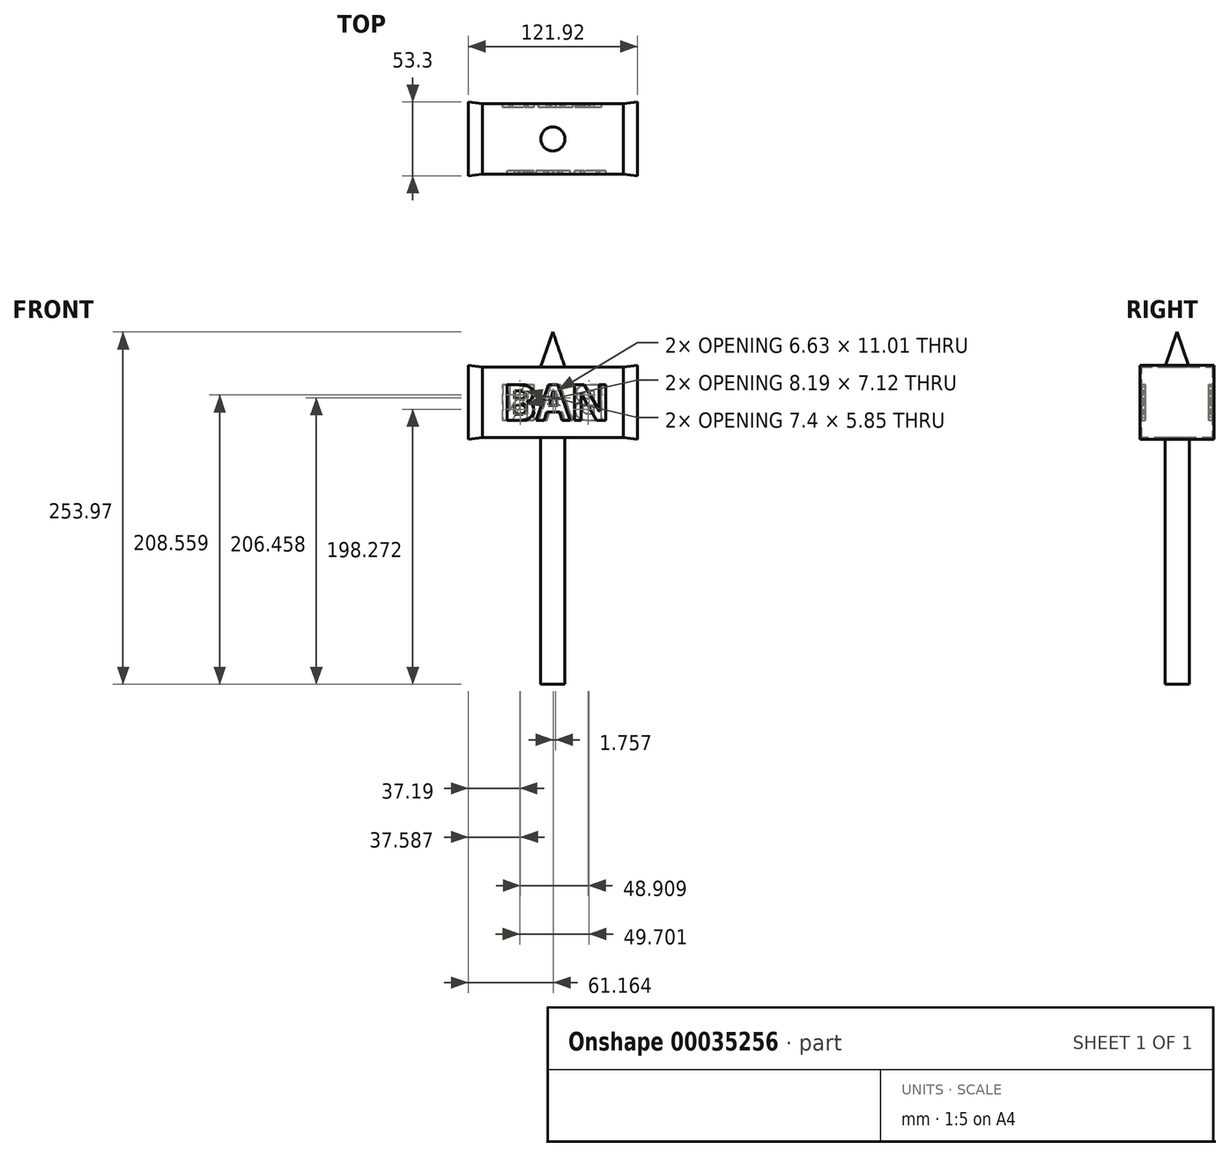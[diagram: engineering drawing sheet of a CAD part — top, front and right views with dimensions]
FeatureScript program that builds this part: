
annotation { "Feature Type Name" : "Feature", "Feature Type Description" : "" }
export const myFeature = defineFeature(function(context is Context, id is Id, definition is map)
    precondition{}
    {
        {
            var Q0;
            Q0=qCreatedBy(makeId("Right.planeOp"),FACE);
            var sketch = newSketch(context, id + "F0", { "sketchPlane" : qUnion([Q0])});
            skLineSegment(sketch, "E0.bottom", {"start": v(-25.4, 25.4) * mm, "end": v(25.4, 25.4) * mm});
            skLineSegment(sketch, "E0.top", {"start": v(-25.4, -25.4) * mm, "end": v(25.4, -25.4) * mm});
            skLineSegment(sketch, "E0.left", {"start": v(-25.4, 25.4) * mm, "end": v(-25.4, -25.4) * mm});
            skLineSegment(sketch, "E0.right", {"start": v(25.4, 25.4) * mm, "end": v(25.4, -25.4) * mm});
            skSolve(sketch);
        }
        {
            var Q0;
            Q0 = qSketchRegion(id + "F0", true);
            extrude(context, id + "F1", {"entities" : qUnion([Q0]), "endBound" : BoundingType.SYMMETRIC, "depth" : 101.6 * mm});
        }
        {
            var Q0;
            Q0=makeQuery(id+"F1.opExtrude","SWEPT_FACE",FACE,{"disambiguationData":[OSD([sQuery(id+"F0.wireOp",EDGE,"E0.right")])]});
            var sketch = newSketch(context, id + "F2", { "sketchPlane" : qUnion([Q0])});
            skLineSegment(sketch, "E1", {"start": v(-50.8, 25.4) * mm, "end": v(-38.23, 12.83) * mm});
            skLineSegment(sketch, "E2.MirrorCS", {"start": v(50.8, 25.4) * mm, "end": v(38.23, 12.83) * mm});
            skLineSegment(sketch, "E3.MirrorCS", {"start": v(-50.8, -25.4) * mm, "end": v(-38.23, -12.83) * mm});
            skLineSegment(sketch, "E4.MirrorCS", {"start": v(50.8, -25.4) * mm, "end": v(36.07, -12.83) * mm});
            skText(sketch, "E5", { "text": "BAN\n", "fontName": "OpenSans-Bold.ttf"});
            const initialGuessF2  = {"E5": [-0.03823, -0.01283, 1, 0, 0.02566]};
            skSetInitialGuess(sketch, initialGuessF2);
            skSolve(sketch);
        }
        {
            var Q0;
            Q0 = qSketchRegion(id + "F2", true);
            extrude(context, id + "F3", {"entities" : qUnion([Q0]), "operationType" : NewBodyOperationType.REMOVE, "oppositeDirection" : true, "depth" : 2.54 * mm});
        }
        {
            var Q0;
            Q0=makeQuery(id+"F1.opExtrude","SWEPT_FACE",FACE,{"disambiguationData":[OSD([sQuery(id+"F0.wireOp",EDGE,"E0.left")])]});
            var sketch = newSketch(context, id + "F4", { "sketchPlane" : qUnion([Q0])});
            skLineSegment(sketch, "E6.0", {"start": v(50.8, 25.4) * mm, "end": v(38.23, 12.83) * mm});
            skLineSegment(sketch, "E7.0.7", {"start": v(20.72, 0.5) * mm, "end": v(20.72, 0.67) * mm});
            skLineSegment(sketch, "E8.0.5", {"start": v(-31.47, -6.44) * mm, "end": v(-31.35, -6.44) * mm});
            skLineSegment(sketch, "E8.0.12", {"start": v(-17.99, 6.41) * mm, "end": v(-18.14, 6.41) * mm});
            skPoint(sketch, "E9", {"position": v(-36.07, -12.83) * mm});
            skPoint(sketch, "E8.0.0.start.orphan", {"position": v(-29.21, -12.83) * mm});
            skPoint(sketch, "E8.0.9.end.orphan", {"position": v(-18.32, -12.83) * mm});
            skPoint(sketch, "E8.0.9.start.orphan", {"position": v(-13.5, -12.83) * mm});
            skPoint(sketch, "E10.0.1.end.orphan", {"position": v(-10.3, -12.83) * mm});
            skPoint(sketch, "E10.0.1.start.orphan", {"position": v(-4.49, -12.83) * mm});
            skPoint(sketch, "E7.0.3.end.orphan", {"position": v(18.68, -10.88) * mm});
            skPoint(sketch, "E7.0.2.end.orphan", {"position": v(25.51, -12.83) * mm});
            skPoint(sketch, "E7.0.2.start.orphan", {"position": v(35.03, -12.83) * mm});
            skPoint(sketch, "E10.0.5.end.orphan", {"position": v(8.47, -12.83) * mm});
            skPoint(sketch, "E10.0.5.start.orphan", {"position": v(14.29, -12.83) * mm});
            skText(sketch, "E11", { "text": "BAN", "fontName": "OpenSans-Bold.ttf"});
            const initialGuessF4  = {"E11": [-0.03607, -0.01283, 1, 0, 0.02566]};
            skSetInitialGuess(sketch, initialGuessF4);
            skSolve(sketch);
        }
        {
            var Q0;
            Q0 = qSketchRegion(id + "F4", true);
            extrude(context, id + "F5", {"entities" : qUnion([Q0]), "operationType" : NewBodyOperationType.REMOVE, "oppositeDirection" : true, "depth" : 2.54 * mm});
        }
        {
            var Q0;
            Q0=makeQuery(id+"F1.opExtrude","CAP_FACE",FACE,{"disambiguationData":[OSD([sQuery(id+"F0.wireOp",EDGE,"E0.bottom"),sQuery(id+"F0.wireOp",EDGE,"E0.top"),sQuery(id+"F0.wireOp",EDGE,"E0.left"),sQuery(id+"F0.wireOp",EDGE,"E0.right")])],"isStart":true});
            var sketch = newSketch(context, id + "F6", { "sketchPlane" : qUnion([Q0])});
            skLineSegment(sketch, "E12.0", {"start": v(25.4, 25.4) * mm, "end": v(-25.4, 25.4) * mm});
            skLineSegment(sketch, "E12.1", {"start": v(25.4, 25.4) * mm, "end": v(25.4, -25.4) * mm});
            skSolve(sketch);
        }
        {
            var Q0;
            Q0=makeQuery(id+"F6.imprint","IMPRINT",FACE,{"disambiguationData":[TD([[makeQuery(id+"F6.imprint","IMPRINT",EDGE,{"derivedFrom":sQuery(id+"F6.wireOp",EDGE,"E12.0")}),1.0]])]});
            extrude(context, id + "F7", {"entities" : qUnion([Q0]), "depth" : 10.16 * mm, "hasDraft" : true, "draftAngle" : 7 * degree});
        }
        {
            var Q0;
            Q0=makeQuery(id+"F1.opExtrude","CAP_FACE",FACE,{"disambiguationData":[OSD([sQuery(id+"F0.wireOp",EDGE,"E0.bottom"),sQuery(id+"F0.wireOp",EDGE,"E0.top"),sQuery(id+"F0.wireOp",EDGE,"E0.left"),sQuery(id+"F0.wireOp",EDGE,"E0.right")])],"isStart":false});
            extrude(context, id + "F8", {"entities" : qUnion([Q0]), "depth" : 10.16 * mm, "hasDraft" : true, "draftAngle" : 7 * degree});
        }
        {
            var Q0;
            Q0=makeQuery(id+"F1.opExtrude","SWEPT_FACE",FACE,{"disambiguationData":[OSD([sQuery(id+"F0.wireOp",EDGE,"E0.top")])]});
            var sketch = newSketch(context, id + "F9", { "sketchPlane" : qUnion([Q0])});
            skCircle(sketch, "E13", {"center": v(0, 0) * mm, "radius": 8.73 * mm});
            skSolve(sketch);
        }
        {
            var Q0;
            Q0 = qSketchRegion(id + "F9", true);
            extrude(context, id + "F10", {"entities" : qUnion([Q0]), "depth" : 177.8 * mm});
        }
        {
            var Q0;
            Q0=makeQuery(id+"F1.opExtrude","SWEPT_FACE",FACE,{"disambiguationData":[OSD([sQuery(id+"F0.wireOp",EDGE,"E0.bottom")])]});
            var sketch = newSketch(context, id + "F11", { "sketchPlane" : qUnion([Q0])});
            skCircle(sketch, "E14.0", {"center": v(0, 0) * mm, "radius": 8.73 * mm});
            skSolve(sketch);
        }
        {
            var Q0;
            Q0 = qSketchRegion(id + "F11", true);
            extrude(context, id + "F12", {"entities" : qUnion([Q0]), "depth" : 25.4 * mm, "hasDraft" : true, "draftAngle" : 19 * degree, "draftPullDirection" : true});
        }
        {
            var Q0;
            Q0=makeQuery(id+"F5.boolean.opBoolean","COPY",FACE,{"derivedFrom":makeQuery(id+"F5.opExtrude","CAP_FACE",FACE,{"disambiguationData":[OSD([sQuery(id+"F4.wireOp",EDGE,"E11.sketch_text.stroke-0"),sQuery(id+"F4.wireOp",EDGE,"E11.sketch_text.stroke-1"),sQuery(id+"F4.wireOp",EDGE,"E11.sketch_text.stroke-2"),sQuery(id+"F4.wireOp",EDGE,"E11.sketch_text.stroke-3"),sQuery(id+"F4.wireOp",EDGE,"E11.sketch_text.stroke-4"),sQuery(id+"F4.wireOp",EDGE,"E11.sketch_text.stroke-5"),sQuery(id+"F4.wireOp",EDGE,"E11.sketch_text.stroke-6"),sQuery(id+"F4.wireOp",EDGE,"E11.sketch_text.stroke-7"),sQuery(id+"F4.wireOp",EDGE,"E11.sketch_text.stroke-8"),sQuery(id+"F4.wireOp",EDGE,"E11.sketch_text.stroke-9"),sQuery(id+"F4.wireOp",EDGE,"E11.sketch_text.stroke-10"),sQuery(id+"F4.wireOp",EDGE,"E11.sketch_text.stroke-11"),sQuery(id+"F4.wireOp",EDGE,"E11.sketch_text.stroke-12"),sQuery(id+"F4.wireOp",EDGE,"E11.sketch_text.stroke-13"),sQuery(id+"F4.wireOp",EDGE,"E11.sketch_text.stroke-14"),sQuery(id+"F4.wireOp",EDGE,"E11.sketch_text.stroke-15"),sQuery(id+"F4.wireOp",EDGE,"E11.sketch_text.stroke-16"),sQuery(id+"F4.wireOp",EDGE,"E11.sketch_text.stroke-17"),sQuery(id+"F4.wireOp",EDGE,"E11.sketch_text.stroke-18"),sQuery(id+"F4.wireOp",EDGE,"E11.sketch_text.stroke-19"),sQuery(id+"F4.wireOp",EDGE,"E11.sketch_text.stroke-20"),sQuery(id+"F4.wireOp",EDGE,"E11.sketch_text.stroke-21"),sQuery(id+"F4.wireOp",EDGE,"E11.sketch_text.stroke-22"),sQuery(id+"F4.wireOp",EDGE,"E11.sketch_text.stroke-23"),sQuery(id+"F4.wireOp",EDGE,"E11.sketch_text.stroke-24")])],"isStart":false})});
            var sketch = newSketch(context, id + "F13", { "sketchPlane" : qUnion([Q0])});
            skLineSegment(sketch, "E15.0.0", {"start": v(-24.95, 12.61) * mm, "end": v(-32.86, 12.61) * mm});
            skLineSegment(sketch, "E15.0.1", {"start": v(-32.86, 12.61) * mm, "end": v(-32.86, -12.83) * mm});
            skLineSegment(sketch, "E15.0.2", {"start": v(-32.86, -12.83) * mm, "end": v(-23.35, -12.83) * mm});
            skFitSpline(sketch, "E15.0.3", {"points": [v(-23.35, -12.83) * mm, v(-19.03, -12.83) * mm, v(-16.52, -10.88) * mm]});
            skFitSpline(sketch, "E15.0.4", {"points": [v(-16.52, -10.88) * mm, v(-14, -8.93) * mm, v(-14, -5.45) * mm]});
            skFitSpline(sketch, "E15.0.5", {"points": [v(-14, -5.45) * mm, v(-14, -3) * mm, v(-15.07, -1.52) * mm]});
            skFitSpline(sketch, "E15.0.6", {"points": [v(-15.07, -1.52) * mm, v(-16.15, -0.04) * mm, v(-18.56, 0.5) * mm]});
            skLineSegment(sketch, "E15.0.7", {"start": v(-18.56, 0.5) * mm, "end": v(-18.56, 0.67) * mm});
            skFitSpline(sketch, "E15.0.8", {"points": [v(-18.56, 0.67) * mm, v(-16.79, 0.97) * mm, v(-15.72, 2.43) * mm]});
            skFitSpline(sketch, "E15.0.9", {"points": [v(-15.72, 2.43) * mm, v(-14.65, 3.9) * mm, v(-14.65, 6.17) * mm]});
            skFitSpline(sketch, "E15.0.10", {"points": [v(-14.65, 6.17) * mm, v(-14.65, 9.53) * mm, v(-17.1, 11.07) * mm]});
            skFitSpline(sketch, "E15.0.11", {"points": [v(-17.1, 11.07) * mm, v(-19.54, 12.61) * mm, v(-24.95, 12.61) * mm]});
            skLineSegment(sketch, "E16.0.0", {"start": v(4.8, -6.77) * mm, "end": v(6.65, -12.83) * mm});
            skLineSegment(sketch, "E16.0.1", {"start": v(6.65, -12.83) * mm, "end": v(12.46, -12.83) * mm});
            skLineSegment(sketch, "E16.0.2", {"start": v(12.46, -12.83) * mm, "end": v(3.45, 12.72) * mm});
            skLineSegment(sketch, "E16.0.3", {"start": v(3.45, 12.72) * mm, "end": v(-3.14, 12.72) * mm});
            skLineSegment(sketch, "E16.0.4", {"start": v(-3.14, 12.72) * mm, "end": v(-12.13, -12.83) * mm});
            skLineSegment(sketch, "E16.0.5", {"start": v(-12.13, -12.83) * mm, "end": v(-6.31, -12.83) * mm});
            skLineSegment(sketch, "E16.0.6", {"start": v(-6.31, -12.83) * mm, "end": v(-4.47, -6.77) * mm});
            skLineSegment(sketch, "E16.0.7", {"start": v(-4.47, -6.77) * mm, "end": v(4.8, -6.77) * mm});
            skLineSegment(sketch, "E17.0.0", {"start": v(31.37, -12.83) * mm, "end": v(38.23, -12.83) * mm});
            skLineSegment(sketch, "E17.0.1", {"start": v(38.23, -12.83) * mm, "end": v(38.23, 12.61) * mm});
            skLineSegment(sketch, "E17.0.2", {"start": v(38.23, 12.61) * mm, "end": v(33.37, 12.61) * mm});
            skLineSegment(sketch, "E17.0.3", {"start": v(33.37, 12.61) * mm, "end": v(33.37, 0.57) * mm});
            skFitSpline(sketch, "E17.0.4", {"points": [v(33.37, 0.57) * mm, v(33.37, -1.48) * mm, v(33.63, -6.44) * mm]});
            skLineSegment(sketch, "E17.0.5", {"start": v(33.63, -6.44) * mm, "end": v(33.51, -6.44) * mm});
            skLineSegment(sketch, "E17.0.6", {"start": v(33.51, -6.44) * mm, "end": v(22.47, 12.61) * mm});
            skLineSegment(sketch, "E17.0.7", {"start": v(22.47, 12.61) * mm, "end": v(15.66, 12.61) * mm});
            skLineSegment(sketch, "E17.0.8", {"start": v(15.66, 12.61) * mm, "end": v(15.66, -12.83) * mm});
            skLineSegment(sketch, "E17.0.9", {"start": v(15.66, -12.83) * mm, "end": v(20.48, -12.83) * mm});
            skLineSegment(sketch, "E17.0.10", {"start": v(20.48, -12.83) * mm, "end": v(20.48, -0.86) * mm});
            skFitSpline(sketch, "E17.0.11", {"points": [v(20.48, -0.86) * mm, v(20.48, 1.32) * mm, v(20.15, 6.41) * mm]});
            skLineSegment(sketch, "E17.0.12", {"start": v(20.15, 6.41) * mm, "end": v(20.3, 6.41) * mm});
            skLineSegment(sketch, "E17.0.13", {"start": v(20.3, 6.41) * mm, "end": v(31.37, -12.83) * mm});
            skLineSegment(sketch, "E18.0.0", {"start": v(-27.47, 2.53) * mm, "end": v(-24.34, 2.53) * mm});
            skFitSpline(sketch, "E18.0.1", {"points": [v(-24.34, 2.53) * mm, v(-22.15, 2.53) * mm, v(-21.16, 3.21) * mm]});
            skFitSpline(sketch, "E18.0.2", {"points": [v(-21.16, 3.21) * mm, v(-20.18, 3.9) * mm, v(-20.18, 5.46) * mm]});
            skFitSpline(sketch, "E18.0.3", {"points": [v(-20.18, 5.46) * mm, v(-20.18, 6.92) * mm, v(-21.25, 7.56) * mm]});
            skFitSpline(sketch, "E18.0.4", {"points": [v(-21.25, 7.56) * mm, v(-22.32, 8.19) * mm, v(-24.64, 8.19) * mm]});
            skLineSegment(sketch, "E18.0.5", {"start": v(-24.64, 8.19) * mm, "end": v(-27.47, 8.19) * mm});
            skLineSegment(sketch, "E18.0.6", {"start": v(-27.47, 8.19) * mm, "end": v(-27.47, 2.53) * mm});
            skLineSegment(sketch, "E19.0.0", {"start": v(-27.47, -1.74) * mm, "end": v(-27.47, -8.37) * mm});
            skLineSegment(sketch, "E19.0.1", {"start": v(-27.47, -8.37) * mm, "end": v(-23.96, -8.37) * mm});
            skFitSpline(sketch, "E19.0.2", {"points": [v(-23.96, -8.37) * mm, v(-21.73, -8.37) * mm, v(-20.67, -7.52) * mm]});
            skFitSpline(sketch, "E19.0.3", {"points": [v(-20.67, -7.52) * mm, v(-19.6, -6.67) * mm, v(-19.6, -4.91) * mm]});
            skFitSpline(sketch, "E19.0.4", {"points": [v(-19.6, -4.91) * mm, v(-19.6, -1.74) * mm, v(-24.13, -1.74) * mm]});
            skLineSegment(sketch, "E19.0.5", {"start": v(-24.13, -1.74) * mm, "end": v(-27.47, -1.74) * mm});
            skFitSpline(sketch, "E20.0.0", {"points": [v(3.51, -2.25) * mm, v(0.96, 5.98) * mm, v(0.64, 7.06) * mm]});
            skFitSpline(sketch, "E20.0.1", {"points": [v(0.64, 7.06) * mm, v(0.31, 8.14) * mm, v(0.17, 8.76) * mm]});
            skFitSpline(sketch, "E20.0.2", {"points": [v(0.17, 8.76) * mm, v(-0.4, 6.54) * mm, v(-3.11, -2.25) * mm]});
            skLineSegment(sketch, "E20.0.3", {"start": v(-3.11, -2.25) * mm, "end": v(3.51, -2.25) * mm});
            skSolve(sketch);
        }
        {
            var Q0;
            Q0 = qSketchRegion(id + "F13", true);
            extrude(context, id + "F14", {"entities" : qUnion([Q0]), "depth" : 2.54 * mm});
        }
        {
            var Q0;
            Q0=makeQuery(id+"F3.boolean.opBoolean","COPY",FACE,{"derivedFrom":makeQuery(id+"F3.opExtrude","CAP_FACE",FACE,{"disambiguationData":[OSD([sQuery(id+"F2.wireOp",EDGE,"E5.sketch_text.stroke-0"),sQuery(id+"F2.wireOp",EDGE,"E5.sketch_text.stroke-1"),sQuery(id+"F2.wireOp",EDGE,"E5.sketch_text.stroke-2"),sQuery(id+"F2.wireOp",EDGE,"E5.sketch_text.stroke-3"),sQuery(id+"F2.wireOp",EDGE,"E5.sketch_text.stroke-4"),sQuery(id+"F2.wireOp",EDGE,"E5.sketch_text.stroke-5"),sQuery(id+"F2.wireOp",EDGE,"E5.sketch_text.stroke-6"),sQuery(id+"F2.wireOp",EDGE,"E5.sketch_text.stroke-7"),sQuery(id+"F2.wireOp",EDGE,"E5.sketch_text.stroke-8"),sQuery(id+"F2.wireOp",EDGE,"E5.sketch_text.stroke-9"),sQuery(id+"F2.wireOp",EDGE,"E5.sketch_text.stroke-10"),sQuery(id+"F2.wireOp",EDGE,"E5.sketch_text.stroke-11"),sQuery(id+"F2.wireOp",EDGE,"E5.sketch_text.stroke-12"),sQuery(id+"F2.wireOp",EDGE,"E5.sketch_text.stroke-13"),sQuery(id+"F2.wireOp",EDGE,"E5.sketch_text.stroke-14"),sQuery(id+"F2.wireOp",EDGE,"E5.sketch_text.stroke-15"),sQuery(id+"F2.wireOp",EDGE,"E5.sketch_text.stroke-16"),sQuery(id+"F2.wireOp",EDGE,"E5.sketch_text.stroke-17"),sQuery(id+"F2.wireOp",EDGE,"E5.sketch_text.stroke-18"),sQuery(id+"F2.wireOp",EDGE,"E5.sketch_text.stroke-19"),sQuery(id+"F2.wireOp",EDGE,"E5.sketch_text.stroke-20"),sQuery(id+"F2.wireOp",EDGE,"E5.sketch_text.stroke-21"),sQuery(id+"F2.wireOp",EDGE,"E5.sketch_text.stroke-22"),sQuery(id+"F2.wireOp",EDGE,"E5.sketch_text.stroke-23"),sQuery(id+"F2.wireOp",EDGE,"E5.sketch_text.stroke-24")])],"isStart":false})});
            var sketch = newSketch(context, id + "F15", { "sketchPlane" : qUnion([Q0])});
            skLineSegment(sketch, "E21.0.0", {"start": v(-27.1, 12.61) * mm, "end": v(-35.03, 12.61) * mm});
            skLineSegment(sketch, "E21.0.1", {"start": v(-35.03, 12.61) * mm, "end": v(-35.03, -12.83) * mm});
            skLineSegment(sketch, "E21.0.2", {"start": v(-35.03, -12.83) * mm, "end": v(-25.51, -12.83) * mm});
            skFitSpline(sketch, "E21.0.3", {"points": [v(-25.51, -12.83) * mm, v(-21.2, -12.83) * mm, v(-18.68, -10.88) * mm]});
            skFitSpline(sketch, "E21.0.4", {"points": [v(-18.68, -10.88) * mm, v(-16.16, -8.93) * mm, v(-16.16, -5.45) * mm]});
            skFitSpline(sketch, "E21.0.5", {"points": [v(-16.16, -5.45) * mm, v(-16.16, -3) * mm, v(-17.24, -1.52) * mm]});
            skFitSpline(sketch, "E21.0.6", {"points": [v(-17.24, -1.52) * mm, v(-18.3, -0.04) * mm, v(-20.72, 0.5) * mm]});
            skLineSegment(sketch, "E21.0.7", {"start": v(-20.72, 0.5) * mm, "end": v(-20.72, 0.67) * mm});
            skFitSpline(sketch, "E21.0.8", {"points": [v(-20.72, 0.67) * mm, v(-18.95, 0.97) * mm, v(-17.88, 2.43) * mm]});
            skFitSpline(sketch, "E21.0.9", {"points": [v(-17.88, 2.43) * mm, v(-16.8, 3.9) * mm, v(-16.8, 6.17) * mm]});
            skFitSpline(sketch, "E21.0.10", {"points": [v(-16.8, 6.17) * mm, v(-16.8, 9.53) * mm, v(-19.25, 11.07) * mm]});
            skFitSpline(sketch, "E21.0.11", {"points": [v(-19.25, 11.07) * mm, v(-21.7, 12.61) * mm, v(-27.1, 12.61) * mm]});
            skLineSegment(sketch, "E22.0.0", {"start": v(-29.63, 8.19) * mm, "end": v(-29.63, 2.53) * mm});
            skLineSegment(sketch, "E22.0.1", {"start": v(-29.63, 2.53) * mm, "end": v(-26.5, 2.53) * mm});
            skFitSpline(sketch, "E22.0.2", {"points": [v(-26.5, 2.53) * mm, v(-24.3, 2.53) * mm, v(-23.33, 3.21) * mm]});
            skFitSpline(sketch, "E22.0.3", {"points": [v(-23.33, 3.21) * mm, v(-22.34, 3.9) * mm, v(-22.34, 5.46) * mm]});
            skFitSpline(sketch, "E22.0.4", {"points": [v(-22.34, 5.46) * mm, v(-22.34, 6.92) * mm, v(-23.41, 7.56) * mm]});
            skFitSpline(sketch, "E22.0.5", {"points": [v(-23.41, 7.56) * mm, v(-24.48, 8.19) * mm, v(-26.8, 8.19) * mm]});
            skLineSegment(sketch, "E22.0.6", {"start": v(-26.8, 8.19) * mm, "end": v(-29.63, 8.19) * mm});
            skLineSegment(sketch, "E23.0.0", {"start": v(-26.3, -1.74) * mm, "end": v(-29.63, -1.74) * mm});
            skLineSegment(sketch, "E23.0.1", {"start": v(-29.63, -1.74) * mm, "end": v(-29.63, -8.37) * mm});
            skLineSegment(sketch, "E23.0.2", {"start": v(-29.63, -8.37) * mm, "end": v(-26.12, -8.37) * mm});
            skFitSpline(sketch, "E23.0.3", {"points": [v(-26.12, -8.37) * mm, v(-23.9, -8.37) * mm, v(-22.83, -7.52) * mm]});
            skFitSpline(sketch, "E23.0.4", {"points": [v(-22.83, -7.52) * mm, v(-21.77, -6.67) * mm, v(-21.77, -4.91) * mm]});
            skFitSpline(sketch, "E23.0.5", {"points": [v(-21.77, -4.91) * mm, v(-21.77, -1.74) * mm, v(-26.3, -1.74) * mm]});
            skLineSegment(sketch, "E24.0.0", {"start": v(2.64, -6.77) * mm, "end": v(4.49, -12.83) * mm});
            skLineSegment(sketch, "E24.0.1", {"start": v(4.49, -12.83) * mm, "end": v(10.3, -12.83) * mm});
            skLineSegment(sketch, "E24.0.2", {"start": v(10.3, -12.83) * mm, "end": v(1.29, 12.72) * mm});
            skLineSegment(sketch, "E24.0.3", {"start": v(1.29, 12.72) * mm, "end": v(-5.3, 12.72) * mm});
            skLineSegment(sketch, "E24.0.4", {"start": v(-5.3, 12.72) * mm, "end": v(-14.29, -12.83) * mm});
            skLineSegment(sketch, "E24.0.5", {"start": v(-14.29, -12.83) * mm, "end": v(-8.47, -12.83) * mm});
            skLineSegment(sketch, "E24.0.6", {"start": v(-8.47, -12.83) * mm, "end": v(-6.63, -6.77) * mm});
            skLineSegment(sketch, "E24.0.7", {"start": v(-6.63, -6.77) * mm, "end": v(2.64, -6.77) * mm});
            skPoint(sketch, "E25.0", {"position": v(0, 0) * mm});
            skLineSegment(sketch, "E26.0.0", {"start": v(29.21, -12.83) * mm, "end": v(36.07, -12.83) * mm});
            skLineSegment(sketch, "E26.0.1", {"start": v(36.07, -12.83) * mm, "end": v(36.07, 12.61) * mm});
            skLineSegment(sketch, "E26.0.2", {"start": v(36.07, 12.61) * mm, "end": v(31.21, 12.61) * mm});
            skLineSegment(sketch, "E26.0.3", {"start": v(31.21, 12.61) * mm, "end": v(31.21, 0.57) * mm});
            skFitSpline(sketch, "E26.0.4", {"points": [v(31.21, 0.57) * mm, v(31.21, -1.48) * mm, v(31.47, -6.44) * mm]});
            skLineSegment(sketch, "E26.0.5", {"start": v(31.47, -6.44) * mm, "end": v(31.35, -6.44) * mm});
            skLineSegment(sketch, "E26.0.6", {"start": v(31.35, -6.44) * mm, "end": v(20.3, 12.61) * mm});
            skLineSegment(sketch, "E26.0.7", {"start": v(20.3, 12.61) * mm, "end": v(13.5, 12.61) * mm});
            skLineSegment(sketch, "E26.0.8", {"start": v(13.5, 12.61) * mm, "end": v(13.5, -12.83) * mm});
            skLineSegment(sketch, "E26.0.9", {"start": v(13.5, -12.83) * mm, "end": v(18.32, -12.83) * mm});
            skLineSegment(sketch, "E26.0.10", {"start": v(18.32, -12.83) * mm, "end": v(18.32, -0.86) * mm});
            skFitSpline(sketch, "E26.0.11", {"points": [v(18.32, -0.86) * mm, v(18.32, 1.32) * mm, v(17.99, 6.41) * mm]});
            skLineSegment(sketch, "E26.0.12", {"start": v(17.99, 6.41) * mm, "end": v(18.14, 6.41) * mm});
            skLineSegment(sketch, "E26.0.13", {"start": v(18.14, 6.41) * mm, "end": v(29.21, -12.83) * mm});
            skLineSegment(sketch, "E27.0.0", {"start": v(-5.27, -2.25) * mm, "end": v(1.35, -2.25) * mm});
            skFitSpline(sketch, "E27.0.1", {"points": [v(1.35, -2.25) * mm, v(-1.2, 5.98) * mm, v(-1.53, 7.06) * mm]});
            skFitSpline(sketch, "E27.0.2", {"points": [v(-1.53, 7.06) * mm, v(-1.85, 8.14) * mm, v(-1.99, 8.76) * mm]});
            skFitSpline(sketch, "E27.0.3", {"points": [v(-1.99, 8.76) * mm, v(-2.56, 6.54) * mm, v(-5.27, -2.25) * mm]});
            skSolve(sketch);
        }
        {
            var Q0;
            Q0 = qSketchRegion(id + "F15", true);
            extrude(context, id + "F16", {"entities" : qUnion([Q0]), "depth" : 2.54 * mm});
        }
    });
